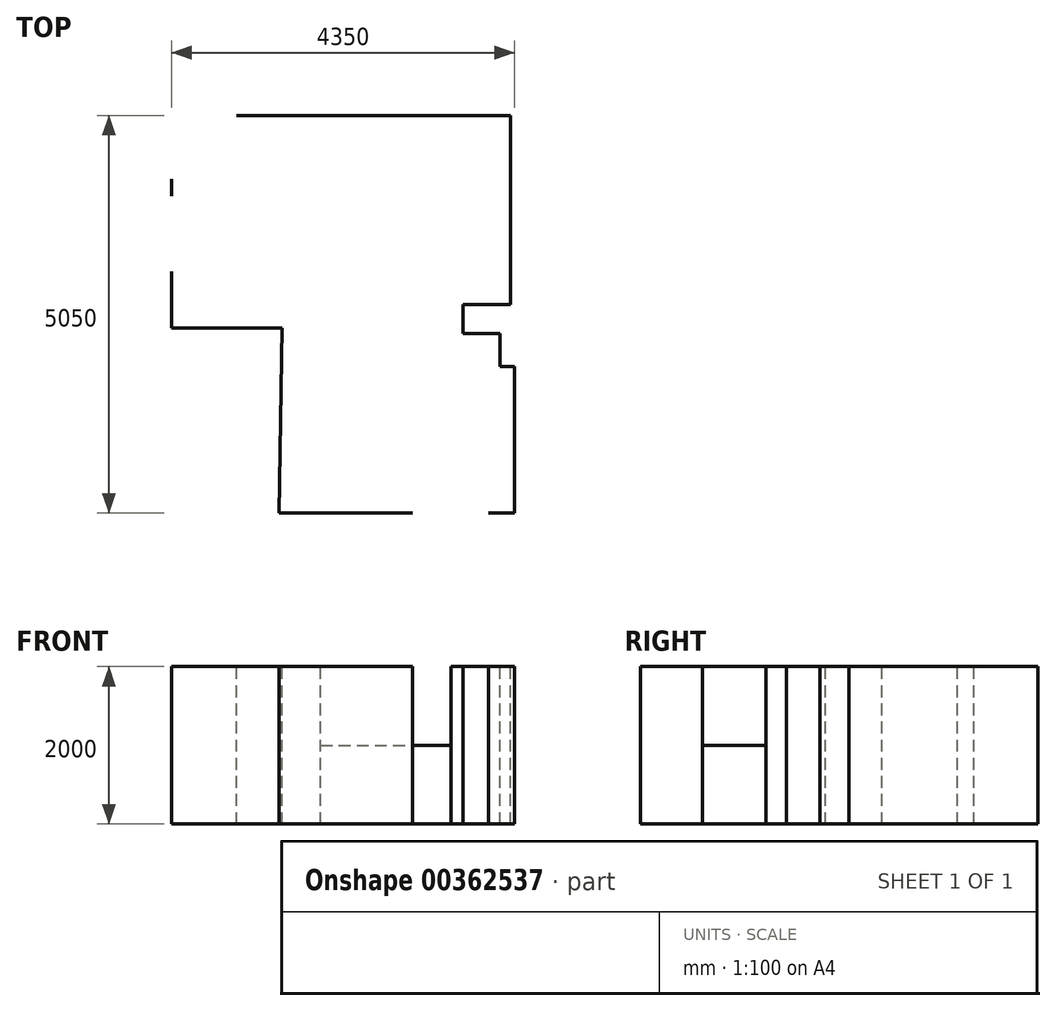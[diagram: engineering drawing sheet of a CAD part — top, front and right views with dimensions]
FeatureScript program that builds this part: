
annotation { "Feature Type Name" : "Feature", "Feature Type Description" : "" }
export const myFeature = defineFeature(function(context is Context, id is Id, definition is map)
    precondition{}
    {
        {
            var Q0;
            Q0=qCreatedBy(makeId("Top.planeOp"),FACE);
            var sketch = newSketch(context, id + "F0", { "sketchPlane" : qUnion([Q0])});
            skLineSegment(sketch, "E0", {"start": v(-1399.4, 0) * mm, "end": v(0, 0) * mm});
            skLineSegment(sketch, "E1", {"start": v(0, 0) * mm, "end": v(-39.4, -2350) * mm});
            skLineSegment(sketch, "E2", {"start": v(2950.6, -490) * mm, "end": v(2770.6, -490) * mm});
            skLineSegment(sketch, "E3", {"start": v(2770.6, -490) * mm, "end": v(2770.6, -70) * mm});
            skLineSegment(sketch, "E4", {"start": v(2900.6, 300) * mm, "end": v(2900.6, 2700) * mm});
            skPoint(sketch, "E5", {"position": v(-1399.4, 2700) * mm});
            skPoint(sketch, "E6", {"position": v(-579.4, 2700) * mm});
            skPoint(sketch, "E7", {"position": v(490.6, 2700) * mm});
            skPoint(sketch, "E8", {"position": v(2150.6, 2700) * mm});
            skPoint(sketch, "E9", {"position": v(-1399.4, 1890) * mm});
            skPoint(sketch, "E10", {"position": v(-1399.4, 1680) * mm});
            skPoint(sketch, "E11", {"position": v(-1399.4, 720) * mm});
            skLineSegment(sketch, "E12", {"start": v(2900.6, 300) * mm, "end": v(2300.6, 300) * mm});
            skLineSegment(sketch, "E13", {"start": v(2300.6, -70) * mm, "end": v(2300.6, 300) * mm});
            skLineSegment(sketch, "E14", {"start": v(2300.6, -70) * mm, "end": v(2770.6, -70) * mm});
            skLineSegment(sketch, "E15", {"start": v(2950.6, -490) * mm, "end": v(2950.6, -750) * mm});
            skLineSegment(sketch, "E16", {"start": v(-579.4, 2700) * mm, "end": v(490.6, 2700) * mm});
            skLineSegment(sketch, "E17", {"start": v(2150.6, 2700) * mm, "end": v(2900.6, 2700) * mm});
            skLineSegment(sketch, "E18", {"start": v(-1399.4, 1890) * mm, "end": v(-1399.4, 1680) * mm});
            skLineSegment(sketch, "E19", {"start": v(-1399.4, 720) * mm, "end": v(-1399.4, 0) * mm});
            skLineSegment(sketch, "E20", {"start": v(2950.6, -1560) * mm, "end": v(2950.6, -2350) * mm});
            skLineSegment(sketch, "E21", {"start": v(2950.6, -2350) * mm, "end": v(2620.6, -2350) * mm});
            skPoint(sketch, "E22", {"position": v(1660.6, -2350) * mm});
            skLineSegment(sketch, "E23", {"start": v(1660.6, -2350) * mm, "end": v(-39.4, -2350) * mm});
            skLineSegment(sketch, "E24", {"start": v(490.6, 2700) * mm, "end": v(2150.6, 2700) * mm});
            skLineSegment(sketch, "E25", {"start": v(-1399.4, 2700) * mm, "end": v(-579.4, 2700) * mm});
            skLineSegment(sketch, "E26", {"start": v(-1399.4, 2700) * mm, "end": v(-1399.4, 1890) * mm});
            skLineSegment(sketch, "E27", {"start": v(-1399.4, 1680) * mm, "end": v(-1399.4, 720) * mm});
            skLineSegment(sketch, "E28", {"start": v(2950.6, -750) * mm, "end": v(2950.6, -1560) * mm});
            skLineSegment(sketch, "E29", {"start": v(2620.6, -2350) * mm, "end": v(1660.6, -2350) * mm});
            skSolve(sketch);
        }
        {
            var Q0;
            Q0=makeQuery(id+"F0.imprint","IMPRINT",FACE,{"disambiguationData":[TD([[makeQuery(id+"F0.imprint","IMPRINT",EDGE,{"derivedFrom":sQuery(id+"F0.wireOp",EDGE,"E0")}),1.0]])]});
            var Q1;
            Q1=sQuery(id+"F0.wireOp",EDGE,"E17");
            var Q2;
            Q2=sQuery(id+"F0.wireOp",EDGE,"E4");
            var Q3;
            Q3=sQuery(id+"F0.wireOp",EDGE,"E12");
            var Q4;
            Q4=sQuery(id+"F0.wireOp",EDGE,"E13");
            var Q5;
            Q5=sQuery(id+"F0.wireOp",EDGE,"E14");
            var Q6;
            Q6=sQuery(id+"F0.wireOp",EDGE,"E3");
            var Q7;
            Q7=sQuery(id+"F0.wireOp",EDGE,"E2");
            var Q8;
            Q8=sQuery(id+"F0.wireOp",EDGE,"E15");
            var Q9;
            Q9=sQuery(id+"F0.wireOp",EDGE,"E20");
            var Q10;
            Q10=sQuery(id+"F0.wireOp",EDGE,"E21");
            var Q11;
            Q11=sQuery(id+"F0.wireOp",EDGE,"E23");
            var Q12;
            Q12=sQuery(id+"F0.wireOp",EDGE,"E1");
            var Q13;
            Q13=sQuery(id+"F0.wireOp",EDGE,"E0");
            var Q14;
            Q14=sQuery(id+"F0.wireOp",EDGE,"E19");
            var Q15;
            Q15=sQuery(id+"F0.wireOp",EDGE,"E18");
            var Q16;
            Q16=sQuery(id+"F0.wireOp",EDGE,"E16");
            extrude(context, id + "F1", {"entities" : qUnion([Q0]), "bodyType" : ToolBodyType.SURFACE, "surfaceEntities" : qUnion([Q1, Q2, Q3, Q4, Q5, Q6, Q7, Q8, Q9, Q10, Q11, Q12, Q13, Q14, Q15, Q16]), "depth" : 2000 * mm});
        }
        {
            var Q0;
            Q0=sQuery(id+"F0.wireOp",EDGE,"E24");
            var Q1;
            Q1=sQuery(id+"F0.wireOp",EDGE,"E28");
            extrude(context, id + "F2", {"bodyType" : ToolBodyType.SURFACE, "surfaceEntities" : qUnion([Q0, Q1]), "depth" : 1000 * mm});
        }
    });
